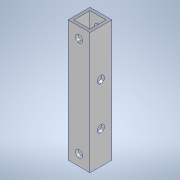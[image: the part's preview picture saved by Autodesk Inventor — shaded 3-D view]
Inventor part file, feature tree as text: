
AUTODESK INVENTOR PART (.ipt)
format: ipt  version: 2020.3 (Build 243373000, 373)  size: 129,536 bytes
history: native  units: mm
features: sketch x3, hole x2, other x1, extrude x1
ambient origin geometry x8: Origin, YZ Plane, XZ Plane, XY Plane, X Axis, Y Axis, Z Axis, Center Point
bodies: Body1 (feature_tree)
feature tree (7):
  other  "ソリッド1"
  extrude  "押し出し1"  Depth=9.0mm
  hole  "穴1"  [1 undecoded]
  hole  "穴2"  [1 undecoded]
  sketch  "スケッチ1"
  sketch  "スケッチ2"
  sketch  "スケッチ3"
note: 2 required parameter values undecoded (feature->parameter linkage not recoverable at this tier; creation-order binding heuristic only, values carry confidence <= 0.55)
